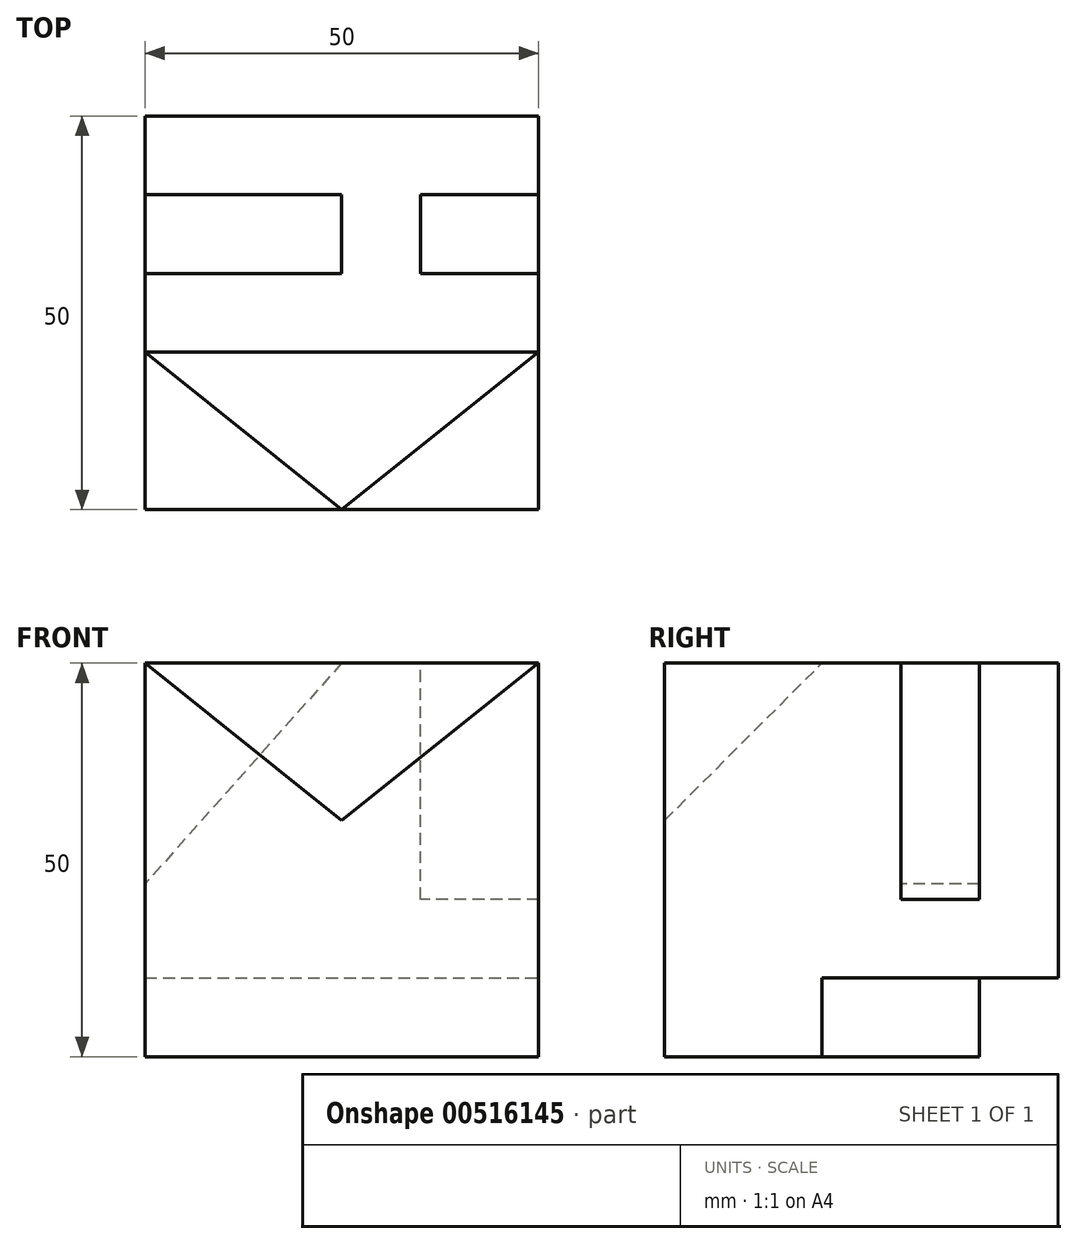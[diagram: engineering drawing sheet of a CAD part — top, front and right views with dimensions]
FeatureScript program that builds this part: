
annotation { "Feature Type Name" : "Feature", "Feature Type Description" : "" }
export const myFeature = defineFeature(function(context is Context, id is Id, definition is map)
    precondition{}
    {
        {
            var Q0;
            Q0=qCreatedBy(makeId("Front.planeOp"),FACE);
            var sketch = newSketch(context, id + "F0", { "sketchPlane" : qUnion([Q0])});
            skLineSegment(sketch, "E0.bottom", {"start": v(0, 0) * mm, "end": v(50, 0) * mm});
            skLineSegment(sketch, "E0.top", {"start": v(0, 50) * mm, "end": v(50, 50) * mm});
            skLineSegment(sketch, "E0.left", {"start": v(0, 0) * mm, "end": v(0, 50) * mm});
            skLineSegment(sketch, "E0.right", {"start": v(50, 0) * mm, "end": v(50, 50) * mm});
            skSolve(sketch);
        }
        {
            var Q0;
            Q0 = qSketchRegion(id + "F0", true);
            extrude(context, id + "F1", {"entities" : qUnion([Q0]), "depth" : 50 * mm, "offsetDistance" : 25 * mm});
        }
        {
            var Q0;
            Q0=makeQuery(id+"F1.opExtrude","CAP_FACE",FACE,{"disambiguationData":[OSD([sQuery(id+"F0.wireOp",EDGE,"E0.bottom"),sQuery(id+"F0.wireOp",EDGE,"E0.top"),sQuery(id+"F0.wireOp",EDGE,"E0.left"),sQuery(id+"F0.wireOp",EDGE,"E0.right")])],"isStart":false});
            var sketch = newSketch(context, id + "F2", { "sketchPlane" : qUnion([Q0])});
            skLineSegment(sketch, "E1", {"start": v(0, 50) * mm, "end": v(25, 30) * mm});
            skLineSegment(sketch, "E2", {"start": v(25, 30) * mm, "end": v(50, 50) * mm});
            skSolve(sketch);
        }
        {
            var Q0;
            Q0=makeQuery(id+"F1.opExtrude","SWEPT_FACE",FACE,{"disambiguationData":[OSD([sQuery(id+"F0.wireOp",EDGE,"E0.top")])]});
            var sketch = newSketch(context, id + "F3", { "sketchPlane" : qUnion([Q0])});
            skLineSegment(sketch, "E3.bottom", {"start": v(0, -50) * mm, "end": v(50, -50) * mm});
            skLineSegment(sketch, "E3.top", {"start": v(0, -30) * mm, "end": v(50, -30) * mm});
            skLineSegment(sketch, "E3.left", {"start": v(0, -50) * mm, "end": v(0, -30) * mm});
            skLineSegment(sketch, "E3.right", {"start": v(50, -50) * mm, "end": v(50, -30) * mm});
            skSolve(sketch);
        }
        {
            var Q0;
            {var subQ0=sQuery(id+"F3.wireOp",EDGE,"E3.top");Q0=makeQuery(id+"F3.imprint","IMPRINT",FACE,{"disambiguationData":[TD([[makeQuery(id+"F3.imprint","IMPRINT",EDGE,{"derivedFrom":subQ0}),1.0]])]});}
            var sketch = newSketch(context, id + "F4", { "sketchPlane" : qUnion([Q0])});
            skLineSegment(sketch, "E4.bottom", {"start": v(0, -10) * mm, "end": v(25, -10) * mm});
            skLineSegment(sketch, "E4.top", {"start": v(0, -20) * mm, "end": v(25, -20) * mm});
            skLineSegment(sketch, "E4.left", {"start": v(0, -10) * mm, "end": v(0, -20) * mm});
            skLineSegment(sketch, "E4.right", {"start": v(25, -10) * mm, "end": v(25, -20) * mm});
            skSolve(sketch);
        }
        {
            var Q0;
            {var subQ0=sQuery(id+"F3.wireOp",EDGE,"E3.top");Q0=makeQuery(id+"F3.imprint","IMPRINT",FACE,{"disambiguationData":[TD([[makeQuery(id+"F3.imprint","IMPRINT",EDGE,{"derivedFrom":subQ0}),1.0]])]});}
            var sketch = newSketch(context, id + "F5", { "sketchPlane" : qUnion([Q0])});
            skLineSegment(sketch, "E5.bottom", {"start": v(50, -10) * mm, "end": v(35, -10) * mm});
            skLineSegment(sketch, "E5.top", {"start": v(50, -20) * mm, "end": v(35, -20) * mm});
            skLineSegment(sketch, "E5.left", {"start": v(50, -10) * mm, "end": v(50, -20) * mm});
            skLineSegment(sketch, "E5.right", {"start": v(35, -10) * mm, "end": v(35, -20) * mm});
            skSolve(sketch);
        }
        {
            var Q0;
            Q0=makeQuery(id+"F1.opExtrude","CAP_FACE",FACE,{"disambiguationData":[OSD([sQuery(id+"F0.wireOp",EDGE,"E0.bottom"),sQuery(id+"F0.wireOp",EDGE,"E0.top"),sQuery(id+"F0.wireOp",EDGE,"E0.left"),sQuery(id+"F0.wireOp",EDGE,"E0.right")])],"isStart":true});
            var sketch = newSketch(context, id + "F6", { "sketchPlane" : qUnion([Q0])});
            skLineSegment(sketch, "E6", {"start": v(-35, 50) * mm, "end": v(-50, 20) * mm});
            skSolve(sketch);
        }
        {
            var Q0;
            Q0=makeQuery(id+"F1.opExtrude","CAP_FACE",FACE,{"disambiguationData":[OSD([sQuery(id+"F0.wireOp",EDGE,"E0.bottom"),sQuery(id+"F0.wireOp",EDGE,"E0.top"),sQuery(id+"F0.wireOp",EDGE,"E0.left"),sQuery(id+"F0.wireOp",EDGE,"E0.right")])],"isStart":true});
            var sketch = newSketch(context, id + "F7", { "sketchPlane" : qUnion([Q0])});
            skLineSegment(sketch, "E7", {"start": v(-25, 50) * mm, "end": v(0, 21.92) * mm});
            skSolve(sketch);
        }
        {
            var Q0;
            Q0=makeQuery(id+"F4.imprint","IMPRINT",FACE,{"disambiguationData":[TD([[makeQuery(id+"F4.imprint","IMPRINT",EDGE,{"derivedFrom":sQuery(id+"F4.wireOp",EDGE,"E4.bottom")}),-1.0]])]});
            var Q1;
            Q1=sQuery(id+"F7.wireOp",EDGE,"E7");
            sweep(context, id + "F8", {"operationType" : NewBodyOperationType.REMOVE, "profiles" : qUnion([Q0]), "path" : qUnion([Q1])});
        }
        {
            var Q0;
            Q0=makeQuery(id+"F5.imprint","IMPRINT",FACE,{"disambiguationData":[TD([[makeQuery(id+"F5.imprint","IMPRINT",EDGE,{"derivedFrom":sQuery(id+"F5.wireOp",EDGE,"E5.bottom")}),1.0]])]});
            extrude(context, id + "F9", {"entities" : qUnion([Q0]), "operationType" : NewBodyOperationType.REMOVE, "oppositeDirection" : true, "depth" : 30 * mm, "offsetDistance" : 25 * mm});
        }
        {
            var Q0;
            Q0=makeQuery(id+"F1.opExtrude","SWEPT_FACE",FACE,{"disambiguationData":[OSD([sQuery(id+"F0.wireOp",EDGE,"E0.bottom")])]});
            var sketch = newSketch(context, id + "F10", { "sketchPlane" : qUnion([Q0])});
            skLineSegment(sketch, "E8", {"start": v(50, 30) * mm, "end": v(0, 10) * mm});
            skSolve(sketch);
        }
        {
            var Q0;
            {var subQ0=sQuery(id+"F10.wireOp",EDGE,"E8");Q0=makeQuery(id+"F10.imprint","IMPRINT",FACE,{"disambiguationData":[TD([[makeQuery(id+"F10.imprint","IMPRINT",EDGE,{"derivedFrom":subQ0}),1.0]])]});}
            extrude(context, id + "F11", {"entities" : qUnion([Q0]), "operationType" : NewBodyOperationType.REMOVE, "oppositeDirection" : true, "depth" : 10 * mm, "offsetDistance" : 25 * mm});
        }
        {
            var Q0;
            Q0=sQuery(id+"F3.wireOp",VERTEX,"E3.left.end");
            var Q1;
            Q1=sQuery(id+"F2.wireOp",VERTEX,"E2.start");
            var Q2;
            Q2=sQuery(id+"F3.wireOp",VERTEX,"E3.right.end");
            cPlane(context, id + "F12", {"entities" : qUnion([Q0, Q1, Q2]), "cplaneType" : CPlaneType.THREE_POINT, "offset" : 25 * mm, "width" : 150 * mm, "height" : 150 * mm});
        }
        {
            var Q0;
            Q0=makeQuery(id+"F2.imprint","IMPRINT",FACE,{"disambiguationData":[TD([[makeQuery(id+"F2.imprint","IMPRINT",EDGE,{"derivedFrom":sQuery(id+"F2.wireOp",EDGE,"E1")}),1.0]])]});
            var Q1;
            Q1=qCreatedBy(id+"F12.planeOp",FACE);
            extrude(context, id + "F13", {"entities" : qUnion([Q0]), "operationType" : NewBodyOperationType.REMOVE, "endBound" : BoundingType.UP_TO_SURFACE, "oppositeDirection" : true, "depth" : 25 * mm, "endBoundEntityFace" : qUnion([Q1]), "offsetDistance" : 25 * mm});
        }
    });
